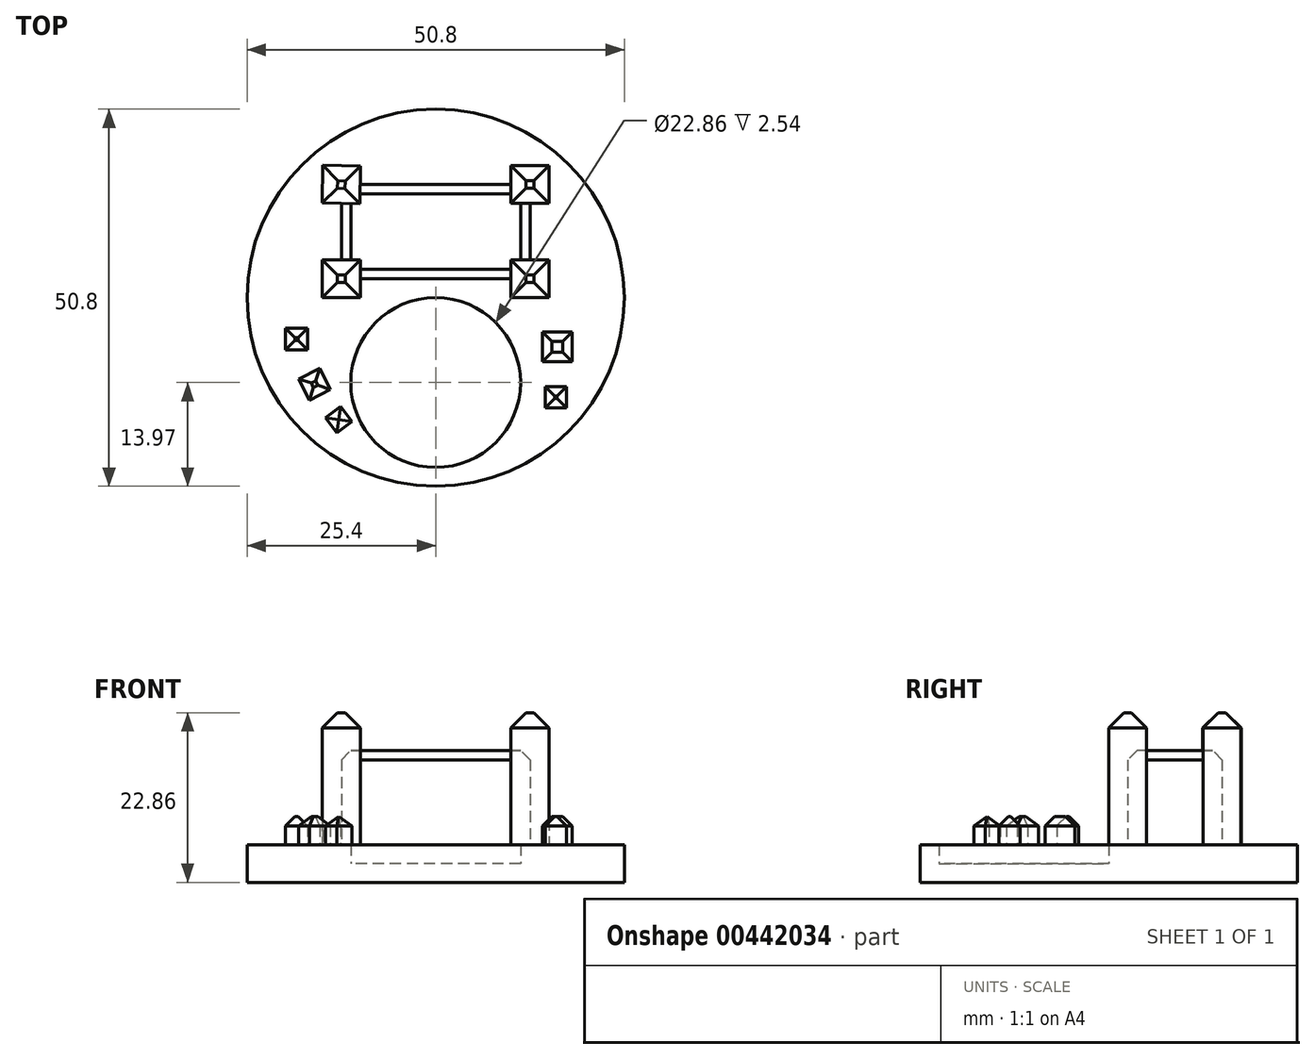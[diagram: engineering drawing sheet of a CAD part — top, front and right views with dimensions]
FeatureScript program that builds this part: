
annotation { "Feature Type Name" : "Feature", "Feature Type Description" : "" }
export const myFeature = defineFeature(function(context is Context, id is Id, definition is map)
    precondition{}
    {
        {
            var Q0;
            Q0=qCreatedBy(makeId("Top.planeOp"),FACE);
            var sketch = newSketch(context, id + "F0", { "sketchPlane" : qUnion([Q0])});
            skCircle(sketch, "E0", {"center": v(0, 0) * mm, "radius": 25.4 * mm});
            skCircle(sketch, "E1", {"center": v(0, -11.43) * mm, "radius": 11.43 * mm});
            skLineSegment(sketch, "E2.bottom", {"start": v(-12.7, 15.24) * mm, "end": v(12.7, 15.24) * mm});
            skLineSegment(sketch, "E2.top", {"start": v(-12.7, 2.54) * mm, "end": v(12.7, 2.54) * mm});
            skLineSegment(sketch, "E2.left", {"start": v(-12.7, 15.24) * mm, "end": v(-12.7, 2.54) * mm});
            skLineSegment(sketch, "E2.right", {"start": v(12.7, 15.24) * mm, "end": v(12.7, 2.54) * mm});
            skPoint(sketch, "E3", {"position": v(0, 15.24) * mm});
            skCircle(sketch, "E4.cCircle", {"center": v(-12.7, 15.24) * mm, "radius": 2.54 * mm, "construction": true});
            skLineSegment(sketch, "E4.0", {"start": v(-15.18, 17.84) * mm, "end": v(-10.1, 17.72) * mm});
            skLineSegment(sketch, "E4.1", {"start": v(-10.1, 17.72) * mm, "end": v(-10.22, 12.64) * mm});
            skLineSegment(sketch, "E4.2", {"start": v(-10.22, 12.64) * mm, "end": v(-15.3, 12.76) * mm});
            skLineSegment(sketch, "E4.3", {"start": v(-15.3, 12.76) * mm, "end": v(-15.18, 17.84) * mm});
            skPoint(sketch, "E4.0.midPoint", {"position": v(-12.64, 17.78) * mm});
            skCircle(sketch, "E5.cCircle", {"center": v(12.7, 15.24) * mm, "radius": 2.54 * mm, "construction": true});
            skLineSegment(sketch, "E5.0", {"start": v(10.16, 17.78) * mm, "end": v(15.24, 17.78) * mm});
            skLineSegment(sketch, "E5.1", {"start": v(15.24, 17.78) * mm, "end": v(15.24, 12.7) * mm});
            skLineSegment(sketch, "E5.2", {"start": v(15.24, 12.7) * mm, "end": v(10.16, 12.7) * mm});
            skLineSegment(sketch, "E5.3", {"start": v(10.16, 12.7) * mm, "end": v(10.16, 17.78) * mm});
            skPoint(sketch, "E5.0.midPoint", {"position": v(12.7, 17.78) * mm});
            skCircle(sketch, "E6.cCircle", {"center": v(12.7, 2.54) * mm, "radius": 2.54 * mm, "construction": true});
            skLineSegment(sketch, "E6.0", {"start": v(15.24, 0) * mm, "end": v(10.16, 0) * mm});
            skLineSegment(sketch, "E6.1", {"start": v(10.16, 0) * mm, "end": v(10.16, 5.08) * mm});
            skLineSegment(sketch, "E6.2", {"start": v(10.16, 5.08) * mm, "end": v(15.24, 5.08) * mm});
            skLineSegment(sketch, "E6.3", {"start": v(15.24, 5.08) * mm, "end": v(15.24, 0) * mm});
            skPoint(sketch, "E6.0.midPoint", {"position": v(12.7, 0) * mm});
            skCircle(sketch, "E7.cCircle", {"center": v(-12.7, 2.54) * mm, "radius": 2.54 * mm, "construction": true});
            skLineSegment(sketch, "E7.0", {"start": v(-10.16, 0) * mm, "end": v(-15.24, 0) * mm});
            skLineSegment(sketch, "E7.1", {"start": v(-15.24, 0) * mm, "end": v(-15.24, 5.08) * mm});
            skLineSegment(sketch, "E7.2", {"start": v(-15.24, 5.08) * mm, "end": v(-10.16, 5.08) * mm});
            skLineSegment(sketch, "E7.3", {"start": v(-10.16, 5.08) * mm, "end": v(-10.16, 0) * mm});
            skPoint(sketch, "E7.0.midPoint", {"position": v(-12.7, 0) * mm});
            skCircle(sketch, "E8.cCircle", {"center": v(16.37, -6.6) * mm, "radius": 2 * mm, "construction": true});
            skLineSegment(sketch, "E8.0", {"start": v(14.36, -4.6) * mm, "end": v(18.37, -4.6) * mm});
            skLineSegment(sketch, "E8.1", {"start": v(18.37, -4.6) * mm, "end": v(18.37, -8.6) * mm});
            skLineSegment(sketch, "E8.2", {"start": v(18.37, -8.6) * mm, "end": v(14.36, -8.6) * mm});
            skLineSegment(sketch, "E8.3", {"start": v(14.36, -8.6) * mm, "end": v(14.36, -4.6) * mm});
            skPoint(sketch, "E8.0.midPoint", {"position": v(16.37, -4.6) * mm});
            skCircle(sketch, "E9.cCircle", {"center": v(16.18, -13.38) * mm, "radius": 1.43 * mm, "construction": true});
            skLineSegment(sketch, "E9.0", {"start": v(14.75, -11.95) * mm, "end": v(17.61, -11.95) * mm});
            skLineSegment(sketch, "E9.1", {"start": v(17.61, -11.95) * mm, "end": v(17.61, -14.8) * mm});
            skLineSegment(sketch, "E9.2", {"start": v(17.61, -14.8) * mm, "end": v(14.75, -14.8) * mm});
            skLineSegment(sketch, "E9.3", {"start": v(14.75, -14.8) * mm, "end": v(14.75, -11.95) * mm});
            skPoint(sketch, "E9.0.midPoint", {"position": v(16.18, -11.95) * mm});
            skCircle(sketch, "E10.cCircle", {"center": v(-18.73, -5.55) * mm, "radius": 1.48 * mm, "construction": true});
            skLineSegment(sketch, "E10.0", {"start": v(-20.21, -4.07) * mm, "end": v(-17.26, -4.07) * mm});
            skLineSegment(sketch, "E10.1", {"start": v(-17.26, -4.07) * mm, "end": v(-17.26, -7.03) * mm});
            skLineSegment(sketch, "E10.2", {"start": v(-17.26, -7.03) * mm, "end": v(-20.21, -7.03) * mm});
            skLineSegment(sketch, "E10.3", {"start": v(-20.21, -7.03) * mm, "end": v(-20.21, -4.07) * mm});
            skPoint(sketch, "E10.0.midPoint", {"position": v(-18.73, -4.07) * mm});
            skCircle(sketch, "E11.cCircle", {"center": v(-16.3, -11.65) * mm, "radius": 1.6 * mm, "construction": true});
            skLineSegment(sketch, "E11.0", {"start": v(-18.45, -10.93) * mm, "end": v(-15.6, -9.5) * mm});
            skLineSegment(sketch, "E11.1", {"start": v(-15.6, -9.5) * mm, "end": v(-14.16, -12.36) * mm});
            skLineSegment(sketch, "E11.2", {"start": v(-14.16, -12.36) * mm, "end": v(-17.02, -13.79) * mm});
            skLineSegment(sketch, "E11.3", {"start": v(-17.02, -13.79) * mm, "end": v(-18.45, -10.93) * mm});
            skPoint(sketch, "E11.0.midPoint", {"position": v(-17.02, -10.22) * mm});
            skCircle(sketch, "E12.cCircle", {"center": v(-13.07, -16.4) * mm, "radius": 1.27 * mm, "construction": true});
            skLineSegment(sketch, "E12.0", {"start": v(-12.82, -14.63) * mm, "end": v(-11.29, -16.65) * mm});
            skLineSegment(sketch, "E12.1", {"start": v(-11.29, -16.65) * mm, "end": v(-13.31, -18.19) * mm});
            skLineSegment(sketch, "E12.2", {"start": v(-13.31, -18.19) * mm, "end": v(-14.85, -16.16) * mm});
            skLineSegment(sketch, "E12.3", {"start": v(-14.85, -16.16) * mm, "end": v(-12.82, -14.63) * mm});
            skPoint(sketch, "E12.0.midPoint", {"position": v(-12.05, -15.64) * mm});
            skSolve(sketch);
        }
        {
            var Q0;
            Q0=makeQuery(id+"F0.imprint","IMPRINT",FACE,{"disambiguationData":[TD([[makeQuery(id+"F0.imprint","IMPRINT",EDGE,{"derivedFrom":sQuery(id+"F0.wireOp",EDGE,"E0")}),1.0]])]});
            extrude(context, id + "F1", {"entities" : qUnion([Q0]), "depth" : 5.08 * mm});
        }
        {
            var Q0;
            Q0=makeQuery(id+"F0.imprint","IMPRINT",FACE,{"disambiguationData":[TD([[makeQuery(id+"F0.imprint","IMPRINT",EDGE,{"derivedFrom":sQuery(id+"F0.wireOp",EDGE,"E1")}),1.0]])]});
            extrude(context, id + "F2", {"entities" : qUnion([Q0]), "operationType" : NewBodyOperationType.ADD, "depth" : 2.54 * mm});
        }
        {
            var Q0;
            {var subQ12=sQuery(id+"F0.wireOp",EDGE,"E2.bottom");var subQ15=sQuery(id+"F0.wireOp",EDGE,"E4.1");var subQ17=makeQuery(id+"F0.imprint","INTERSECT",VERTEX,{"derivedFrom":[subQ12,subQ15]});Q0=makeQuery(id+"F0.imprint","IMPRINT",FACE,{"disambiguationData":[TD([[makeQuery(id+"F0.imprint","IMPRINT",EDGE,{"disambiguationData":[TD([[subQ17,-1.0]])],"derivedFrom":subQ12}),-1.0]])]});}
            extrude(context, id + "F3", {"entities" : qUnion([Q0]), "operationType" : NewBodyOperationType.ADD, "depth" : 17.78 * mm});
        }
        {
            var Q0;
            {var subQ0=sQuery(id+"F0.wireOp",EDGE,"E2.left");var subQ1=sQuery(id+"F0.wireOp",EDGE,"E2.bottom");var subQ2=makeQuery(id+"F0.imprint","INTERSECT",VERTEX,{"derivedFrom":[subQ1,subQ0]});Q0=makeQuery(id+"F0.imprint","IMPRINT",FACE,{"disambiguationData":[TD([[makeQuery(id+"F0.imprint","IMPRINT",EDGE,{"disambiguationData":[TD([[subQ2,-1.0]])],"derivedFrom":subQ1}),-1.0]])]});}
            var Q1;
            {var subQ1=sQuery(id+"F0.wireOp",EDGE,"E4.0");Q1=makeQuery(id+"F0.imprint","IMPRINT",FACE,{"disambiguationData":[TD([[makeQuery(id+"F0.imprint","IMPRINT",EDGE,{"derivedFrom":subQ1}),-1.0]])]});}
            var Q2;
            {var subQ0=sQuery(id+"F0.wireOp",EDGE,"E2.left");var subQ1=sQuery(id+"F0.wireOp",EDGE,"E2.top");var subQ2=makeQuery(id+"F0.imprint","INTERSECT",VERTEX,{"derivedFrom":[subQ1,subQ0]});Q2=makeQuery(id+"F0.imprint","IMPRINT",FACE,{"disambiguationData":[TD([[makeQuery(id+"F0.imprint","IMPRINT",EDGE,{"disambiguationData":[TD([[subQ2,-1.0]])],"derivedFrom":subQ1}),1.0]])]});}
            var Q3;
            {var subQ1=sQuery(id+"F0.wireOp",EDGE,"E7.0");Q3=makeQuery(id+"F0.imprint","IMPRINT",FACE,{"disambiguationData":[TD([[makeQuery(id+"F0.imprint","IMPRINT",EDGE,{"derivedFrom":subQ1}),-1.0]])]});}
            var Q4;
            {var subQ0=sQuery(id+"F0.wireOp",EDGE,"E2.right");var subQ1=sQuery(id+"F0.wireOp",EDGE,"E2.bottom");var subQ2=makeQuery(id+"F0.imprint","INTERSECT",VERTEX,{"derivedFrom":[subQ1,subQ0]});Q4=makeQuery(id+"F0.imprint","IMPRINT",FACE,{"disambiguationData":[TD([[makeQuery(id+"F0.imprint","IMPRINT",EDGE,{"disambiguationData":[TD([[subQ2,1.0]])],"derivedFrom":subQ1}),-1.0]])]});}
            var Q5;
            {var subQ0=sQuery(id+"F0.wireOp",EDGE,"E5.0");Q5=makeQuery(id+"F0.imprint","IMPRINT",FACE,{"disambiguationData":[TD([[makeQuery(id+"F0.imprint","IMPRINT",EDGE,{"derivedFrom":subQ0}),-1.0]])]});}
            var Q6;
            {var subQ0=sQuery(id+"F0.wireOp",EDGE,"E2.right");var subQ1=sQuery(id+"F0.wireOp",EDGE,"E2.top");var subQ2=makeQuery(id+"F0.imprint","INTERSECT",VERTEX,{"derivedFrom":[subQ1,subQ0]});Q6=makeQuery(id+"F0.imprint","IMPRINT",FACE,{"disambiguationData":[TD([[makeQuery(id+"F0.imprint","IMPRINT",EDGE,{"disambiguationData":[TD([[subQ2,1.0]])],"derivedFrom":subQ1}),1.0]])]});}
            var Q7;
            {var subQ0=sQuery(id+"F0.wireOp",EDGE,"E6.0");Q7=makeQuery(id+"F0.imprint","IMPRINT",FACE,{"disambiguationData":[TD([[makeQuery(id+"F0.imprint","IMPRINT",EDGE,{"derivedFrom":subQ0}),-1.0]])]});}
            extrude(context, id + "F4", {"entities" : qUnion([Q0, Q1, Q2, Q3, Q4, Q5, Q6, Q7]), "operationType" : NewBodyOperationType.ADD, "depth" : 22.86 * mm});
        }
        {
            var Q0;
            Q0=makeQuery(id+"F0.imprint","IMPRINT",FACE,{"disambiguationData":[TD([[makeQuery(id+"F0.imprint","IMPRINT",EDGE,{"derivedFrom":sQuery(id+"F0.wireOp",EDGE,"E10.0")}),-1.0]])]});
            var Q1;
            Q1=makeQuery(id+"F0.imprint","IMPRINT",FACE,{"disambiguationData":[TD([[makeQuery(id+"F0.imprint","IMPRINT",EDGE,{"derivedFrom":sQuery(id+"F0.wireOp",EDGE,"E11.0")}),-1.0]])]});
            var Q2;
            Q2=makeQuery(id+"F0.imprint","IMPRINT",FACE,{"disambiguationData":[TD([[makeQuery(id+"F0.imprint","IMPRINT",EDGE,{"derivedFrom":sQuery(id+"F0.wireOp",EDGE,"E12.0")}),-1.0]])]});
            var Q3;
            Q3=makeQuery(id+"F0.imprint","IMPRINT",FACE,{"disambiguationData":[TD([[makeQuery(id+"F0.imprint","IMPRINT",EDGE,{"derivedFrom":sQuery(id+"F0.wireOp",EDGE,"E8.0")}),-1.0]])]});
            var Q4;
            Q4=makeQuery(id+"F0.imprint","IMPRINT",FACE,{"disambiguationData":[TD([[makeQuery(id+"F0.imprint","IMPRINT",EDGE,{"derivedFrom":sQuery(id+"F0.wireOp",EDGE,"E9.0")}),-1.0]])]});
            extrude(context, id + "F5", {"entities" : qUnion([Q0, Q1, Q2, Q3, Q4]), "operationType" : NewBodyOperationType.ADD, "depth" : 8.9 * mm});
        }
        {
            var Q0;
            Q0=makeQuery(id+"F5.opExtrude","CAP_FACE",FACE,{"disambiguationData":[OSD([sQuery(id+"F0.wireOp",EDGE,"E10.0"),sQuery(id+"F0.wireOp",EDGE,"E10.1"),sQuery(id+"F0.wireOp",EDGE,"E10.2"),sQuery(id+"F0.wireOp",EDGE,"E10.3")])],"isStart":false});
            var Q1;
            Q1=makeQuery(id+"F5.opExtrude","CAP_FACE",FACE,{"disambiguationData":[OSD([sQuery(id+"F0.wireOp",EDGE,"E11.0"),sQuery(id+"F0.wireOp",EDGE,"E11.1"),sQuery(id+"F0.wireOp",EDGE,"E11.2"),sQuery(id+"F0.wireOp",EDGE,"E11.3")])],"isStart":false});
            var Q2;
            Q2=makeQuery(id+"F5.opExtrude","CAP_FACE",FACE,{"disambiguationData":[OSD([sQuery(id+"F0.wireOp",EDGE,"E12.0"),sQuery(id+"F0.wireOp",EDGE,"E12.1"),sQuery(id+"F0.wireOp",EDGE,"E12.2"),sQuery(id+"F0.wireOp",EDGE,"E12.3")])],"isStart":false});
            var Q3;
            Q3=makeQuery(id+"F5.opExtrude","CAP_FACE",FACE,{"disambiguationData":[OSD([sQuery(id+"F0.wireOp",EDGE,"E8.0"),sQuery(id+"F0.wireOp",EDGE,"E8.1"),sQuery(id+"F0.wireOp",EDGE,"E8.2"),sQuery(id+"F0.wireOp",EDGE,"E8.3")])],"isStart":false});
            var Q4;
            Q4=makeQuery(id+"F5.opExtrude","CAP_FACE",FACE,{"disambiguationData":[OSD([sQuery(id+"F0.wireOp",EDGE,"E9.0"),sQuery(id+"F0.wireOp",EDGE,"E9.1"),sQuery(id+"F0.wireOp",EDGE,"E9.2"),sQuery(id+"F0.wireOp",EDGE,"E9.3")])],"isStart":false});
            chamfer(context, id + "F6", {"entities" : qUnion([Q0, Q1, Q2, Q3, Q4]), "width" : 1.27 * mm, "tangentPropagation" : true});
        }
        {
            var Q0;
            Q0=makeQuery(id+"F4.opExtrude","CAP_FACE",FACE,{"disambiguationData":[OSD([sQuery(id+"F0.wireOp",EDGE,"E4.0"),sQuery(id+"F0.wireOp",EDGE,"E4.1"),sQuery(id+"F0.wireOp",EDGE,"E4.2"),sQuery(id+"F0.wireOp",EDGE,"E4.3")])],"isStart":false});
            var Q1;
            Q1=makeQuery(id+"F4.opExtrude","CAP_FACE",FACE,{"disambiguationData":[OSD([sQuery(id+"F0.wireOp",EDGE,"E7.0"),sQuery(id+"F0.wireOp",EDGE,"E7.1"),sQuery(id+"F0.wireOp",EDGE,"E7.2"),sQuery(id+"F0.wireOp",EDGE,"E7.3")])],"isStart":false});
            var Q2;
            Q2=makeQuery(id+"F4.opExtrude","CAP_FACE",FACE,{"disambiguationData":[OSD([sQuery(id+"F0.wireOp",EDGE,"E5.0"),sQuery(id+"F0.wireOp",EDGE,"E5.1"),sQuery(id+"F0.wireOp",EDGE,"E5.2"),sQuery(id+"F0.wireOp",EDGE,"E5.3")])],"isStart":false});
            var Q3;
            Q3=makeQuery(id+"F4.opExtrude","CAP_FACE",FACE,{"disambiguationData":[OSD([sQuery(id+"F0.wireOp",EDGE,"E6.0"),sQuery(id+"F0.wireOp",EDGE,"E6.1"),sQuery(id+"F0.wireOp",EDGE,"E6.2"),sQuery(id+"F0.wireOp",EDGE,"E6.3")])],"isStart":false});
            chamfer(context, id + "F7", {"entities" : qUnion([Q0, Q1, Q2, Q3]), "width" : 2.03 * mm, "tangentPropagation" : true});
        }
        {
            var Q0;
            Q0=makeQuery(id+"F3.opExtrude","CAP_EDGE",EDGE,{"disambiguationData":[OSD([sQuery(id+"F0.wireOp",EDGE,"E2.top")])],"isStart":false});
            var Q1;
            Q1=makeQuery(id+"F3.opExtrude","CAP_EDGE",EDGE,{"disambiguationData":[OSD([sQuery(id+"F0.wireOp",EDGE,"E2.bottom")])],"isStart":false});
            var Q2;
            Q2=makeQuery(id+"F3.opExtrude","CAP_EDGE",EDGE,{"disambiguationData":[OSD([sQuery(id+"F0.wireOp",EDGE,"E2.left")])],"isStart":false});
            var Q3;
            Q3=makeQuery(id+"F3.opExtrude","CAP_EDGE",EDGE,{"disambiguationData":[OSD([sQuery(id+"F0.wireOp",EDGE,"E2.right")])],"isStart":false});
            chamfer(context, id + "F8", {"entities" : qUnion([Q0, Q1, Q2, Q3]), "width" : 1.27 * mm, "tangentPropagation" : true});
        }
    });
